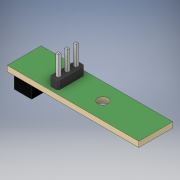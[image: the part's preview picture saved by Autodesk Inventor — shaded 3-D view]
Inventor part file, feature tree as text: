
AUTODESK INVENTOR PART (.ipt)
format: ipt  version: 2019 (Build 230136000, 136)  size: 507,392 bytes
history: native  units: mm
features: extrude x5, sketch x5, other x4, chamfer x2, projected_geometry x2
ambient origin geometry x8: Origin, YZ Plane, XZ Plane, XY Plane, X Axis, Y Axis, Z Axis, Center Point
bodies: Body1 (feature_tree)
feature tree (18):
  other  "Твердое тело1"
  extrude  "Выдавливание1"  Depth=10.0mm
  extrude  "Выдавливание2"  Depth=15.6mm
  chamfer  "Фаска1"  Distance=3.0mm
  extrude  "Выдавливание3"  Depth=1.6mm TaperAngle=0.0deg
  chamfer  "Фаска2"  Distance=2.6mm
  sketch  "Эскиз5"
  extrude  "Выдавливание4"  Depth=8.0mm
  extrude  "Выдавливание5"  Depth=10.9mm
  sketch  "Эскиз2"
  other  "Картинка1"
  sketch  "Эскиз3"
  other  "Картинка2"
  sketch  "Эскиз4"
  projected_geometry  "Спроецированная петля1"
  other  "Картинка3"
  sketch  "Эскиз6"
  projected_geometry  "Спроецированная петля2"
